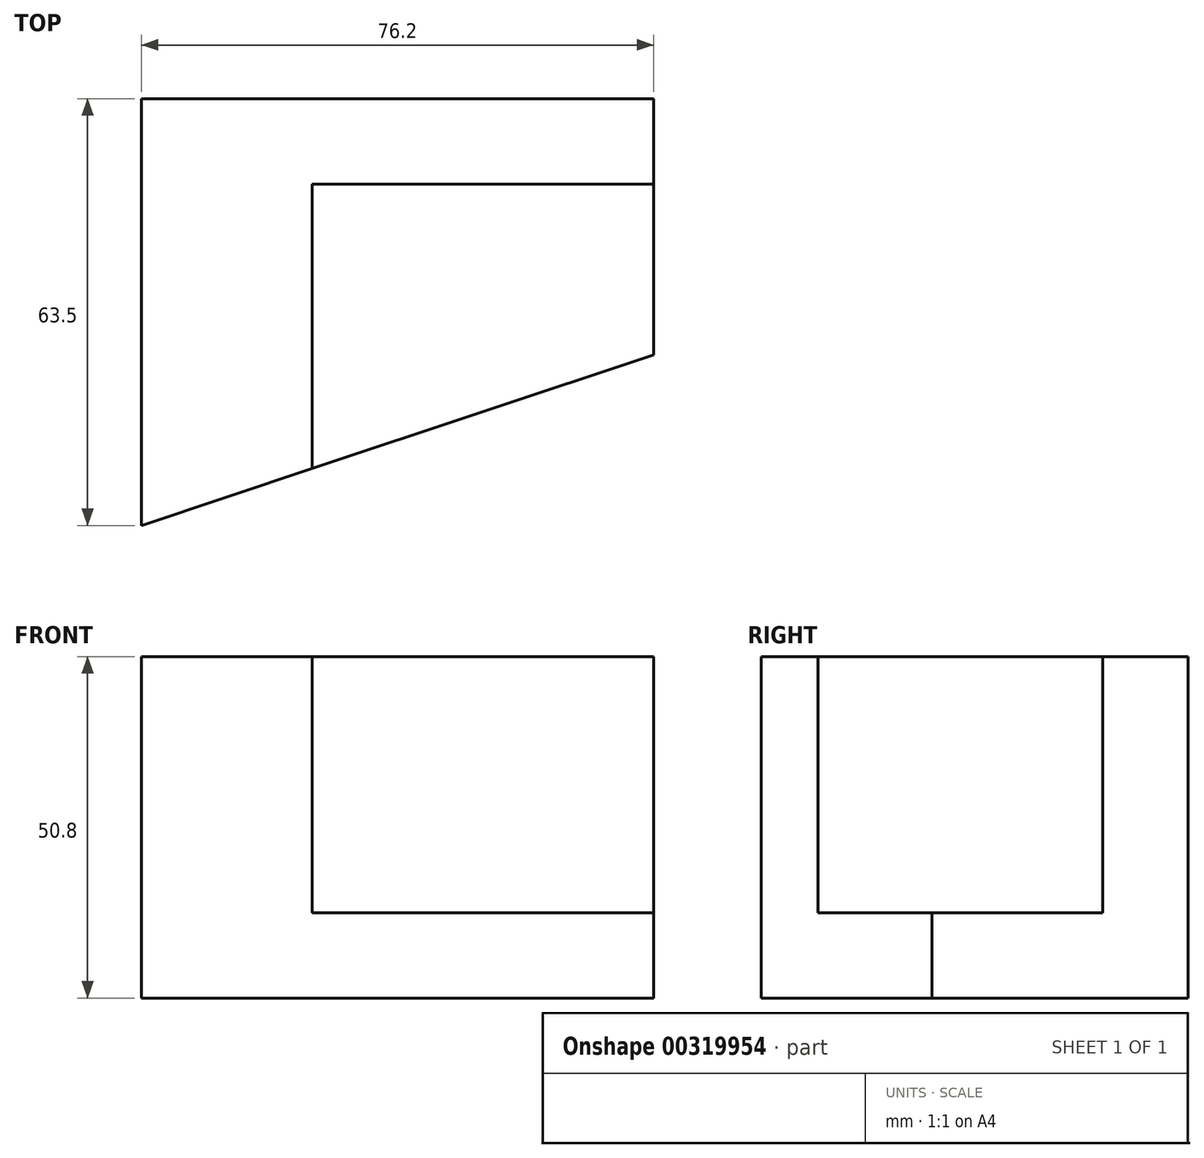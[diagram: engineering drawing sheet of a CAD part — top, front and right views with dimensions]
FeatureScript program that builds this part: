
annotation { "Feature Type Name" : "Feature", "Feature Type Description" : "" }
export const myFeature = defineFeature(function(context is Context, id is Id, definition is map)
    precondition{}
    {
        {
            var Q0;
            Q0=qCreatedBy(makeId("Front.planeOp"),FACE);
            var sketch = newSketch(context, id + "F0", { "sketchPlane" : qUnion([Q0])});
            skLineSegment(sketch, "E0", {"start": v(0, 0) * mm, "end": v(0, 12.7) * mm});
            skLineSegment(sketch, "E1", {"start": v(0, 12.7) * mm, "end": v(76.2, 12.7) * mm});
            skLineSegment(sketch, "E2", {"start": v(76.2, 12.7) * mm, "end": v(76.2, 0) * mm});
            skLineSegment(sketch, "E3", {"start": v(76.2, 0) * mm, "end": v(0, 0) * mm});
            skSolve(sketch);
        }
        {
            var Q0;
            Q0 = qSketchRegion(id + "F0", true);
            extrude(context, id + "F1", {"entities" : qUnion([Q0]), "endBound" : BoundingType.SYMMETRIC, "depth" : 63.5 * mm});
        }
        {
            var Q0;
            Q0=makeQuery(id+"F1.opExtrude","SWEPT_FACE",FACE,{"disambiguationData":[OSD([sQuery(id+"F0.wireOp",EDGE,"E1")])]});
            var sketch = newSketch(context, id + "F2", { "sketchPlane" : qUnion([Q0])});
            skLineSegment(sketch, "E4", {"start": v(0, 31.75) * mm, "end": v(0, 19.05) * mm});
            skLineSegment(sketch, "E5", {"start": v(0, 19.05) * mm, "end": v(76.2, 19.05) * mm});
            skLineSegment(sketch, "E6", {"start": v(76.2, 19.05) * mm, "end": v(76.2, 31.75) * mm});
            skLineSegment(sketch, "E7", {"start": v(76.2, 31.75) * mm, "end": v(0, 31.75) * mm});
            skSolve(sketch);
        }
        {
            var Q0;
            Q0 = qSketchRegion(id + "F2", true);
            extrude(context, id + "F3", {"entities" : qUnion([Q0]), "operationType" : NewBodyOperationType.ADD, "depth" : 38.1 * mm});
        }
        {
            var Q0;
            Q0=makeQuery(id+"F1.opExtrude","SWEPT_FACE",FACE,{"disambiguationData":[OSD([sQuery(id+"F0.wireOp",EDGE,"E1")])]});
            var sketch = newSketch(context, id + "F4", { "sketchPlane" : qUnion([Q0])});
            skLineSegment(sketch, "E8", {"start": v(0, -31.75) * mm, "end": v(0, 19.05) * mm});
            skLineSegment(sketch, "E9", {"start": v(0, 19.05) * mm, "end": v(25.4, 19.05) * mm});
            skLineSegment(sketch, "E10", {"start": v(25.4, 19.05) * mm, "end": v(25.4, -31.75) * mm});
            skLineSegment(sketch, "E11", {"start": v(25.4, -31.75) * mm, "end": v(0, -31.75) * mm});
            skSolve(sketch);
        }
        {
            var Q0;
            Q0 = qSketchRegion(id + "F4", true);
            extrude(context, id + "F5", {"entities" : qUnion([Q0]), "operationType" : NewBodyOperationType.ADD, "depth" : 38.1 * mm});
        }
        {
            var Q0;
            Q0=makeQuery(id+"F1.opExtrude","SWEPT_FACE",FACE,{"disambiguationData":[OSD([sQuery(id+"F0.wireOp",EDGE,"E1")])]});
            var sketch = newSketch(context, id + "F6", { "sketchPlane" : qUnion([Q0])});
            skLineSegment(sketch, "E12", {"start": v(76.2, -31.75) * mm, "end": v(76.2, -6.35) * mm});
            skLineSegment(sketch, "E13", {"start": v(76.2, -6.35) * mm, "end": v(0, -31.75) * mm});
            skLineSegment(sketch, "E14", {"start": v(0, -31.75) * mm, "end": v(76.2, -31.75) * mm});
            skSolve(sketch);
        }
        {
            var Q0;
            Q0 = qSketchRegion(id + "F6", true);
            extrude(context, id + "F7", {"entities" : qUnion([Q0]), "operationType" : NewBodyOperationType.REMOVE, "endBound" : BoundingType.SYMMETRIC, "depth" : 254 * mm});
        }
    });
